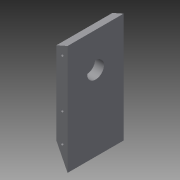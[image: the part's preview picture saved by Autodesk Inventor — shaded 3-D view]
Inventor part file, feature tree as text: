
AUTODESK INVENTOR PART (.ipt)
format: ipt  version: 2015 (Build 190159000, 159)  size: 102,912 bytes
history: native  units: mm
features: extrude x3, sketch x2, plane x1
ambient origin geometry x8: Origin, YZ Plane, XZ Plane, XY Plane, X Axis, Y Axis, Z Axis, Center Point
bodies: Body1 (feature_tree)
feature tree (6):
  sketch  "Sketch1"  dims[d3=10.0mm d4=73.5mm]
  plane  "Work Plane1"
  extrude  "Extrusion3"  Depth=10.0mm
  sketch  "Sketch3"  dims[d6=4.444444mm d8=20.0mm d17=2.5mm d26=2.5mm d28=2.5mm d29=50.0mm d30=0.0mm d37=26.5mm d38=25.0mm d39=15.0mm d40=10.0mm d41=0.0mm d42=8.0mm d43=2.0mm d44=0.0mm]
  extrude  "Extrusion6"  Depth=2.0mm
  extrude  "Extrusion7"  Depth=2.0mm
